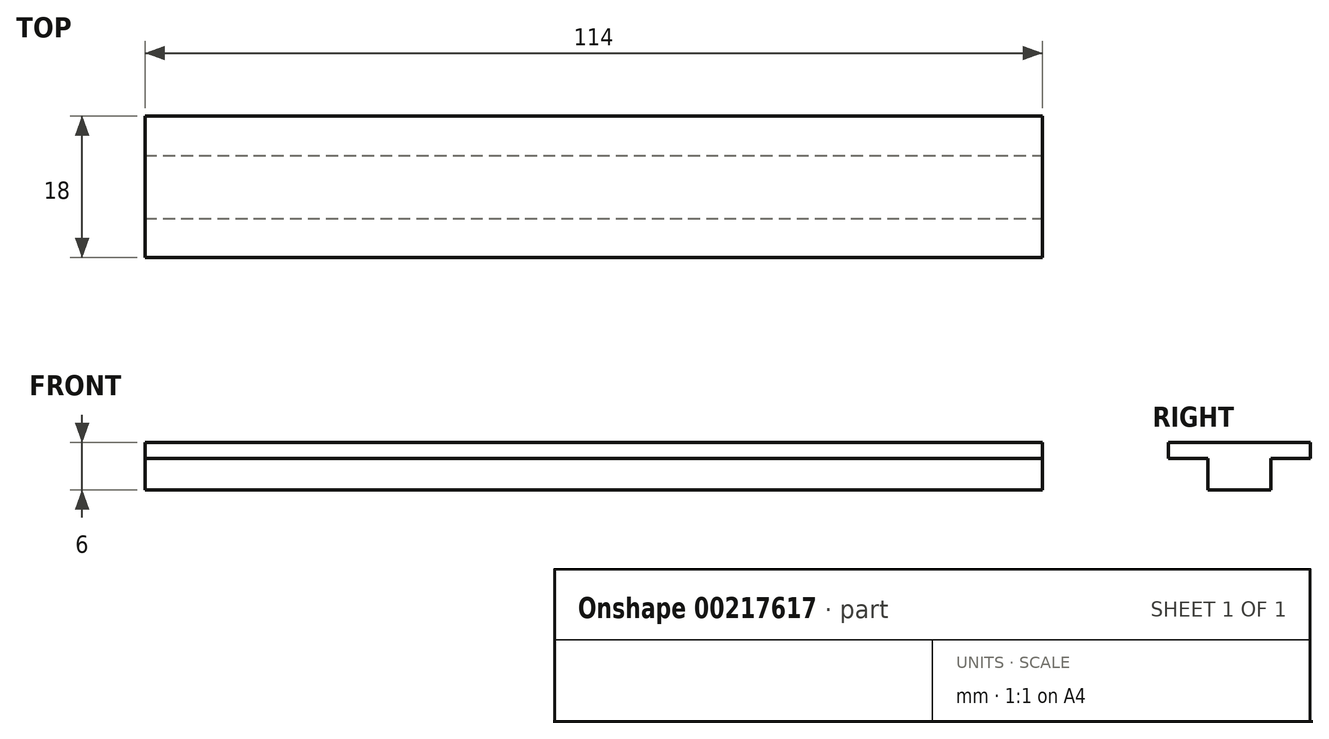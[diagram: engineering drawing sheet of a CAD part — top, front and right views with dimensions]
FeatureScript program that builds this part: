
annotation { "Feature Type Name" : "Feature", "Feature Type Description" : "" }
export const myFeature = defineFeature(function(context is Context, id is Id, definition is map)
    precondition{}
    {
        {
            var Q0;
            Q0=qCreatedBy(makeId("Top.planeOp"),FACE);
            var sketch = newSketch(context, id + "F0", { "sketchPlane" : qUnion([Q0]), "disableImprinting" : false});
            skLineSegment(sketch, "E0.bottom", {"start": v(-55.1, -1.59) * mm, "end": v(58.9, -1.59) * mm});
            skLineSegment(sketch, "E0.top", {"start": v(-55.1, -9.59) * mm, "end": v(58.9, -9.59) * mm});
            skLineSegment(sketch, "E0.left", {"start": v(-55.1, -1.59) * mm, "end": v(-55.1, -9.59) * mm});
            skLineSegment(sketch, "E0.right", {"start": v(58.9, -1.59) * mm, "end": v(58.9, -9.59) * mm});
            skSolve(sketch);
        }
        {
            var Q0;
            Q0 = qSketchRegion(id + "F0", true);
            extrude(context, id + "F1", {"entities" : qUnion([Q0]), "depth" : 4 * mm});
        }
        {
            var Q0;
            Q0=makeQuery(id+"F1.opExtrude","CAP_FACE",FACE,{"disambiguationData":[OSD([sQuery(id+"F0.wireOp",EDGE,"E0.bottom"),sQuery(id+"F0.wireOp",EDGE,"E0.top"),sQuery(id+"F0.wireOp",EDGE,"E0.left"),sQuery(id+"F0.wireOp",EDGE,"E0.right")])],"isStart":false});
            var sketch = newSketch(context, id + "F2", { "sketchPlane" : qUnion([Q0]), "disableImprinting" : false});
            skLineSegment(sketch, "E1.bottom", {"start": v(-55.1, 3.41) * mm, "end": v(58.9, 3.41) * mm});
            skLineSegment(sketch, "E1.top", {"start": v(-55.1, -14.59) * mm, "end": v(58.9, -14.59) * mm});
            skLineSegment(sketch, "E1.left", {"start": v(-55.1, 3.41) * mm, "end": v(-55.1, -14.59) * mm});
            skLineSegment(sketch, "E1.right", {"start": v(58.9, 3.41) * mm, "end": v(58.9, -14.59) * mm});
            skSolve(sketch);
        }
        {
            var Q0;
            {var subQ0=sQuery(id+"F2.wireOp",EDGE,"E1.bottom");Q0=makeQuery(id+"F2.imprint","IMPRINT",FACE,{"disambiguationData":[TD([[makeQuery(id+"F2.imprint","IMPRINT",EDGE,{"derivedFrom":subQ0}),-1.0]])]});}
            var Q1;
            {var subQ1=makeQuery(id+"F1.opExtrude","CAP_EDGE",EDGE,{"disambiguationData":[OSD([sQuery(id+"F0.wireOp",EDGE,"E0.bottom")])],"isStart":false});Q1=makeQuery(id+"F2.imprint","IMPRINT",FACE,{"disambiguationData":[TD([[makeQuery(id+"F2.imprint","IMPRINT",EDGE,{"derivedFrom":subQ1}),-1.0]])]});}
            var Q2;
            {var subQ0=sQuery(id+"F2.wireOp",EDGE,"E1.top");Q2=makeQuery(id+"F2.imprint","IMPRINT",FACE,{"disambiguationData":[TD([[makeQuery(id+"F2.imprint","IMPRINT",EDGE,{"derivedFrom":subQ0}),1.0]])]});}
            extrude(context, id + "F3", {"entities" : qUnion([Q0, Q1, Q2]), "operationType" : NewBodyOperationType.ADD, "depth" : 2 * mm});
        }
    });
